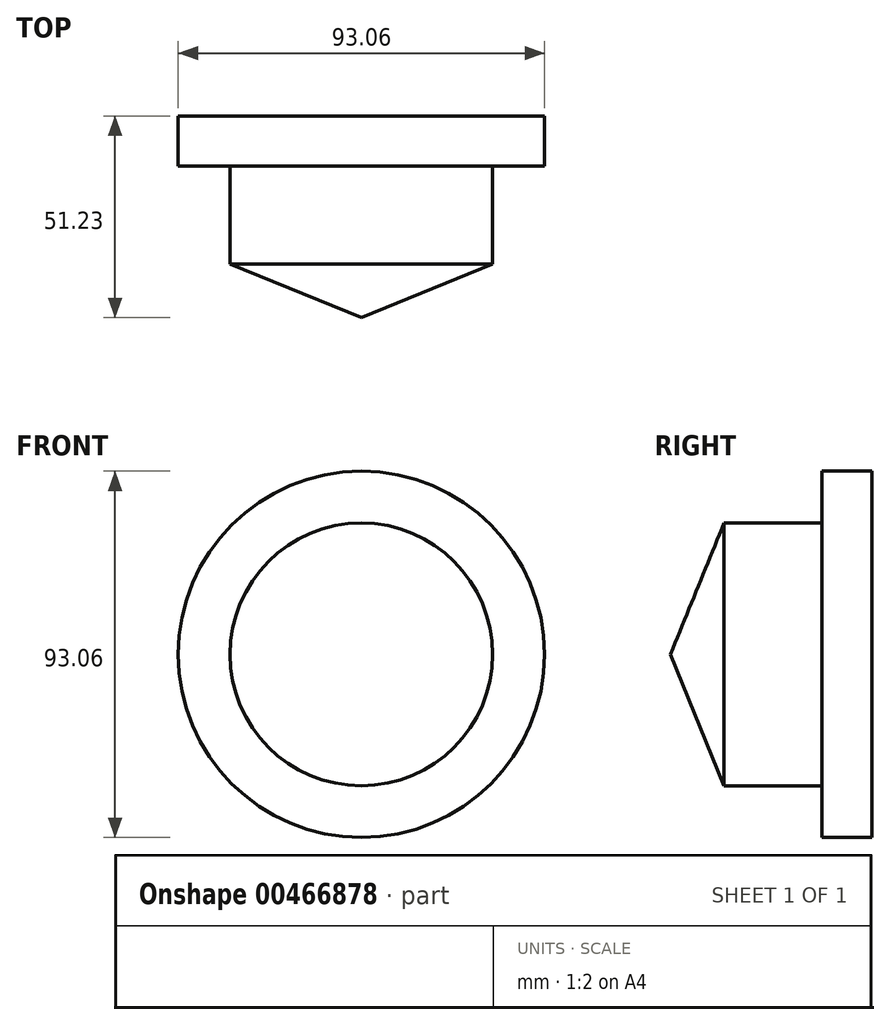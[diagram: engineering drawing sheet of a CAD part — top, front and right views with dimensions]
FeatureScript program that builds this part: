
annotation { "Feature Type Name" : "Feature", "Feature Type Description" : "" }
export const myFeature = defineFeature(function(context is Context, id is Id, definition is map)
    precondition{}
    {
        {
            var Q0;
            Q0=qCreatedBy(makeId("Top.planeOp"),FACE);
            var sketch = newSketch(context, id + "F0", { "sketchPlane" : qUnion([Q0])});
            skLineSegment(sketch, "E0", {"start": v(0, 0) * mm, "end": v(33.37, 13.63) * mm});
            skLineSegment(sketch, "E1", {"start": v(33.37, 13.63) * mm, "end": v(33.37, 38.54) * mm});
            skLineSegment(sketch, "E2", {"start": v(33.37, 38.54) * mm, "end": v(46.53, 38.54) * mm});
            skLineSegment(sketch, "E3", {"start": v(46.53, 38.54) * mm, "end": v(46.53, 51.23) * mm});
            skLineSegment(sketch, "E4", {"start": v(46.53, 51.23) * mm, "end": v(33.37, 51.23) * mm});
            skLineSegment(sketch, "E5", {"start": v(0, 0) * mm, "end": v(0, 51.23) * mm});
            skLineSegment(sketch, "E6", {"start": v(0, 51.23) * mm, "end": v(33.37, 51.23) * mm});
            skLineSegment(sketch, "E7", {"start": v(0, 0) * mm, "end": v(0, -67.68) * mm});
            skLineSegment(sketch, "E8", {"start": v(0, -67.68) * mm, "end": v(42.3, -67.68) * mm});
            skLineSegment(sketch, "E9", {"start": v(42.3, -67.68) * mm, "end": v(42.3, -35.72) * mm});
            skLineSegment(sketch, "E10", {"start": v(0, -35.72) * mm, "end": v(42.3, -35.72) * mm});
            skLineSegment(sketch, "E11", {"start": v(0, -46.53) * mm, "end": v(42.3, -46.53) * mm});
            skLineSegment(sketch, "E12", {"start": v(0, -57.34) * mm, "end": v(42.3, -57.34) * mm});
            skSolve(sketch);
        }
        {
            var Q0;
            Q0=makeQuery(id+"F0.imprint","IMPRINT",FACE,{"disambiguationData":[TD([[makeQuery(id+"F0.imprint","IMPRINT",EDGE,{"derivedFrom":sQuery(id+"F0.wireOp",EDGE,"E0")}),1.0]])]});
            var Q1;
            Q1=sQuery(id+"F0.wireOp",EDGE,"E5");
            revolve(context, id + "F1", {"entities" : qUnion([Q0]), "axis" : qUnion([Q1]), "revolveType" : RevolveType.FULL});
        }
    });
